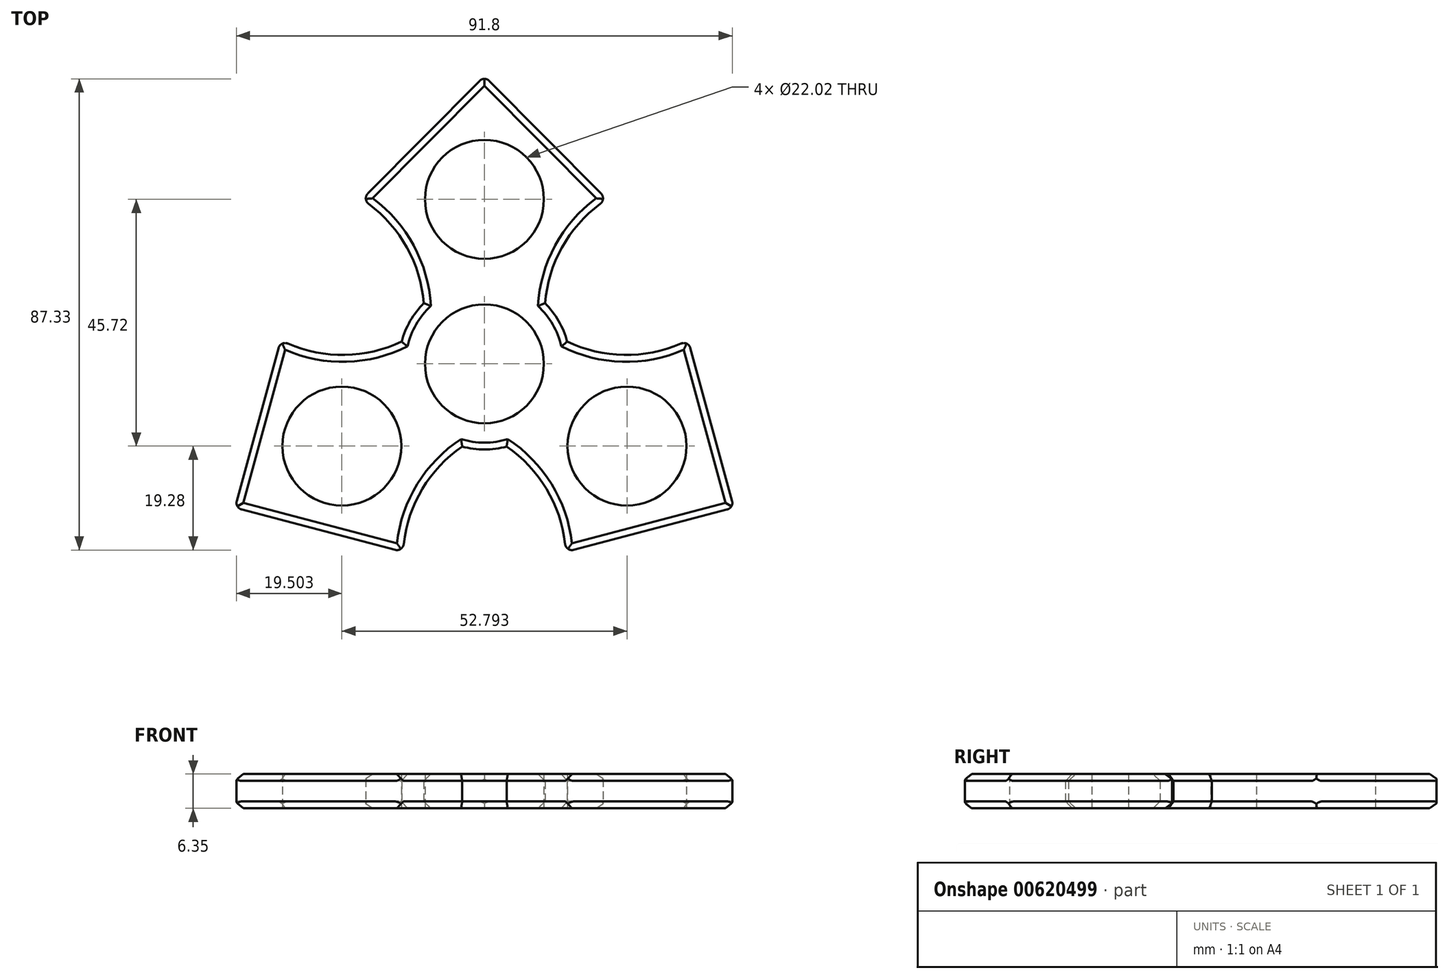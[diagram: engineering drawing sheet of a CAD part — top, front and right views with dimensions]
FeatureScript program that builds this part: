
annotation { "Feature Type Name" : "Feature", "Feature Type Description" : "" }
export const myFeature = defineFeature(function(context is Context, id is Id, definition is map)
    precondition{}
    {
        {
            var Q0;
            Q0=qCreatedBy(makeId("Top.planeOp"),FACE);
            var sketch = newSketch(context, id + "F0", { "sketchPlane" : qUnion([Q0])});
            skCircle(sketch, "E0", {"center": v(0, 0) * mm, "radius": 11.01 * mm});
            skLineSegment(sketch, "E1", {"start": v(0, 0) * mm, "end": v(0, 30.48) * mm});
            skLineSegment(sketch, "E2", {"start": v(0, 0) * mm, "end": v(-26.4, -15.24) * mm});
            skLineSegment(sketch, "E3", {"start": v(0, 0) * mm, "end": v(26.4, -15.24) * mm});
            skCircle(sketch, "E4", {"center": v(0, 0) * mm, "radius": 15.88 * mm});
            skArc(sketch, "E5", {"start": v(-11.23, 11.23) * mm, "mid": v(-14.7, 22.18) * mm, "end": v(-22.65, 30.48) * mm});
            skLineSegment(sketch, "E6", {"start": v(-22.65, 30.48) * mm, "end": v(0, 53.34) * mm});
            skCircle(sketch, "E7", {"center": v(0, 30.48) * mm, "radius": 11.01 * mm});
            skLineSegment(sketch, "E8", {"start": v(0, 53.34) * mm, "end": v(22.65, 30.48) * mm});
            skArc(sketch, "E9", {"start": v(22.65, 30.48) * mm, "mid": v(14.7, 22.18) * mm, "end": v(11.23, 11.23) * mm});
            skLineSegment(sketch, "E10", {"start": v(0, 0) * mm, "end": v(-11.23, 11.23) * mm});
            skLineSegment(sketch, "E11", {"start": v(0, 0) * mm, "end": v(11.23, 11.23) * mm});
            skArc(sketch, "E12.1.0", {"start": v(-4.1, -15.33) * mm, "mid": v(-11.86, -23.82) * mm, "end": v(-15.07, -34.86) * mm});
            skLineSegment(sketch, "E12.1.1", {"start": v(-15.07, -34.86) * mm, "end": v(-46.2, -26.67) * mm});
            skLineSegment(sketch, "E12.1.2", {"start": v(-46.2, -26.67) * mm, "end": v(-37.72, 4.38) * mm});
            skArc(sketch, "E12.1.3", {"start": v(-37.72, 4.38) * mm, "mid": v(-26.56, 1.64) * mm, "end": v(-15.33, 4.1) * mm});
            skCircle(sketch, "E12.1.4", {"center": v(-26.4, -15.24) * mm, "radius": 11.01 * mm});
            skArc(sketch, "E12.2.0", {"start": v(15.33, 4.1) * mm, "mid": v(26.56, 1.64) * mm, "end": v(37.72, 4.38) * mm});
            skLineSegment(sketch, "E12.2.1", {"start": v(37.72, 4.38) * mm, "end": v(46.2, -26.67) * mm});
            skLineSegment(sketch, "E12.2.2", {"start": v(46.2, -26.67) * mm, "end": v(15.07, -34.86) * mm});
            skArc(sketch, "E12.2.3", {"start": v(15.07, -34.86) * mm, "mid": v(11.86, -23.82) * mm, "end": v(4.1, -15.33) * mm});
            skCircle(sketch, "E12.2.4", {"center": v(26.4, -15.24) * mm, "radius": 11.01 * mm});
            skLineSegment(sketch, "E13", {"start": v(0, 53.34) * mm, "end": v(0, 30.48) * mm});
            skLineSegment(sketch, "E14", {"start": v(-29.34, 30.48) * mm, "end": v(31.68, 30.48) * mm});
            skSolve(sketch);
        }
        {
            var Q0;
            {var subQ0=sQuery(id+"F0.wireOp",EDGE,"E12.1.0");Q0=makeQuery(id+"F0.imprint","IMPRINT",FACE,{"disambiguationData":[TD([[makeQuery(id+"F0.imprint","IMPRINT",EDGE,{"derivedFrom":subQ0}),-1.0]])]});}
            var Q1;
            {var subQ0=sQuery(id+"F0.wireOp",EDGE,"E5");Q1=makeQuery(id+"F0.imprint","IMPRINT",FACE,{"disambiguationData":[TD([[makeQuery(id+"F0.imprint","IMPRINT",EDGE,{"derivedFrom":subQ0}),-1.0]])]});}
            var Q2;
            {var subQ0=sQuery(id+"F0.wireOp",EDGE,"E12.2.0");Q2=makeQuery(id+"F0.imprint","IMPRINT",FACE,{"disambiguationData":[TD([[makeQuery(id+"F0.imprint","IMPRINT",EDGE,{"derivedFrom":subQ0}),-1.0]])]});}
            var Q3;
            {var subQ0=sQuery(id+"F0.wireOp",EDGE,"E11");var subQ6=sQuery(id+"F0.wireOp",EDGE,"E0");var subQ8=makeQuery(id+"F0.imprint","INTERSECT",VERTEX,{"derivedFrom":[subQ6,subQ0]});Q3=makeQuery(id+"F0.imprint","IMPRINT",FACE,{"disambiguationData":[TD([[makeQuery(id+"F0.imprint","IMPRINT",EDGE,{"disambiguationData":[TD([[subQ8,1.0]])],"derivedFrom":subQ6}),-1.0]])]});}
            var Q4;
            {var subQ2=sQuery(id+"F0.wireOp",EDGE,"E2");var subQ6=sQuery(id+"F0.wireOp",EDGE,"E0");var subQ8=makeQuery(id+"F0.imprint","INTERSECT",VERTEX,{"derivedFrom":[subQ6,subQ2]});Q4=makeQuery(id+"F0.imprint","IMPRINT",FACE,{"disambiguationData":[TD([[makeQuery(id+"F0.imprint","IMPRINT",EDGE,{"disambiguationData":[TD([[subQ8,-1.0]])],"derivedFrom":subQ6}),-1.0]])]});}
            var Q5;
            {var subQ4=sQuery(id+"F0.wireOp",EDGE,"E10");var subQ6=sQuery(id+"F0.wireOp",EDGE,"E0");var subQ7=makeQuery(id+"F0.imprint","INTERSECT",VERTEX,{"derivedFrom":[subQ6,subQ4]});Q5=makeQuery(id+"F0.imprint","IMPRINT",FACE,{"disambiguationData":[TD([[makeQuery(id+"F0.imprint","IMPRINT",EDGE,{"disambiguationData":[TD([[subQ7,-1.0]])],"derivedFrom":subQ6}),-1.0]])]});}
            var Q6;
            {var subQ0=sQuery(id+"F0.wireOp",EDGE,"E1");var subQ1=sQuery(id+"F0.wireOp",EDGE,"E0");var subQ2=makeQuery(id+"F0.imprint","INTERSECT",VERTEX,{"derivedFrom":[subQ1,subQ0]});Q6=makeQuery(id+"F0.imprint","IMPRINT",FACE,{"disambiguationData":[TD([[makeQuery(id+"F0.imprint","IMPRINT",EDGE,{"disambiguationData":[TD([[subQ2,-1.0]])],"derivedFrom":subQ1}),-1.0]])]});}
            var Q7;
            {var subQ0=sQuery(id+"F0.wireOp",EDGE,"E1");var subQ1=sQuery(id+"F0.wireOp",EDGE,"E0");var subQ2=makeQuery(id+"F0.imprint","INTERSECT",VERTEX,{"derivedFrom":[subQ1,subQ0]});Q7=makeQuery(id+"F0.imprint","IMPRINT",FACE,{"disambiguationData":[TD([[makeQuery(id+"F0.imprint","IMPRINT",EDGE,{"disambiguationData":[TD([[subQ2,1.0]])],"derivedFrom":subQ1}),-1.0]])]});}
            var Q8;
            {var subQ0=sQuery(id+"F0.wireOp",EDGE,"E6");Q8=makeQuery(id+"F0.imprint","IMPRINT",FACE,{"disambiguationData":[TD([[makeQuery(id+"F0.imprint","IMPRINT",EDGE,{"derivedFrom":subQ0}),-1.0]])]});}
            var Q9;
            {var subQ5=sQuery(id+"F0.wireOp",EDGE,"E8");Q9=makeQuery(id+"F0.imprint","IMPRINT",FACE,{"disambiguationData":[TD([[makeQuery(id+"F0.imprint","IMPRINT",EDGE,{"derivedFrom":subQ5}),-1.0]])]});}
            var Q10;
            {var subQ0=sQuery(id+"F0.wireOp",EDGE,"E9");Q10=makeQuery(id+"F0.imprint","IMPRINT",FACE,{"disambiguationData":[TD([[makeQuery(id+"F0.imprint","IMPRINT",EDGE,{"derivedFrom":subQ0}),-1.0]])]});}
            extrude(context, id + "F1", {"entities" : qUnion([Q0, Q1, Q2, Q3, Q4, Q5, Q6, Q7, Q8, Q9, Q10]), "depth" : 6.35 * mm, "offsetDistance" : 25.4 * mm});
        }
        {
            var Q0;
            Q0=makeQuery(id+"F1.opExtrude","CAP_EDGE",EDGE,{"disambiguationData":[OSD([sQuery(id+"F0.wireOp",EDGE,"E12.1.1")])],"isStart":false});
            var Q1;
            Q1=makeQuery(id+"F1.opExtrude","CAP_EDGE",EDGE,{"disambiguationData":[OSD([sQuery(id+"F0.wireOp",EDGE,"E12.1.2")])],"isStart":false});
            var Q2;
            Q2=makeQuery(id+"F1.opExtrude","CAP_EDGE",EDGE,{"disambiguationData":[OSD([sQuery(id+"F0.wireOp",EDGE,"E12.1.0")])],"isStart":false});
            var Q3;
            {var subQ0=sQuery(id+"F0.wireOp",EDGE,"E4");Q3=makeQuery(id+"F1.opExtrude","CAP_EDGE",EDGE,{"disambiguationData":[OSD([subQ0]),TDD([makeQuery(id+"F0.imprint","IMPRINT",EDGE,{"disambiguationData":[TD([[makeQuery(id+"F0.imprint","INTERSECT",VERTEX,{"derivedFrom":[subQ0,sQuery(id+"F0.wireOp",EDGE,"E12.1.0")]}),-1.0]])],"derivedFrom":subQ0})])],"isStart":false});}
            var Q4;
            Q4=makeQuery(id+"F1.opExtrude","CAP_EDGE",EDGE,{"disambiguationData":[OSD([sQuery(id+"F0.wireOp",EDGE,"E12.2.3")])],"isStart":false});
            var Q5;
            {var subQ0=sQuery(id+"F0.wireOp",EDGE,"E4");Q5=makeQuery(id+"F1.opExtrude","CAP_EDGE",EDGE,{"disambiguationData":[OSD([subQ0]),TDD([makeQuery(id+"F0.imprint","IMPRINT",EDGE,{"disambiguationData":[TD([[makeQuery(id+"F0.imprint","INTERSECT",VERTEX,{"derivedFrom":[subQ0,sQuery(id+"F0.wireOp",EDGE,"E12.2.0")]}),-1.0]])],"derivedFrom":subQ0})])],"isStart":false});}
            var Q6;
            Q6=makeQuery(id+"F1.opExtrude","CAP_EDGE",EDGE,{"disambiguationData":[OSD([sQuery(id+"F0.wireOp",EDGE,"E12.2.2")])],"isStart":false});
            var Q7;
            Q7=makeQuery(id+"F1.opExtrude","CAP_EDGE",EDGE,{"disambiguationData":[OSD([sQuery(id+"F0.wireOp",EDGE,"E12.2.1")])],"isStart":false});
            var Q8;
            Q8=makeQuery(id+"F1.opExtrude","CAP_EDGE",EDGE,{"disambiguationData":[OSD([sQuery(id+"F0.wireOp",EDGE,"E12.2.0")])],"isStart":false});
            var Q9;
            Q9=makeQuery(id+"F1.opExtrude","CAP_EDGE",EDGE,{"disambiguationData":[OSD([sQuery(id+"F0.wireOp",EDGE,"E9")])],"isStart":false});
            var Q10;
            Q10=makeQuery(id+"F1.opExtrude","CAP_EDGE",EDGE,{"disambiguationData":[OSD([sQuery(id+"F0.wireOp",EDGE,"E8")])],"isStart":false});
            var Q11;
            Q11=makeQuery(id+"F1.opExtrude","CAP_EDGE",EDGE,{"disambiguationData":[OSD([sQuery(id+"F0.wireOp",EDGE,"E6")])],"isStart":false});
            var Q12;
            Q12=makeQuery(id+"F1.opExtrude","CAP_EDGE",EDGE,{"disambiguationData":[OSD([sQuery(id+"F0.wireOp",EDGE,"E5")])],"isStart":false});
            var Q13;
            Q13=makeQuery(id+"F1.opExtrude","CAP_EDGE",EDGE,{"disambiguationData":[OSD([sQuery(id+"F0.wireOp",EDGE,"E12.1.3")])],"isStart":false});
            var Q14;
            {var subQ0=sQuery(id+"F0.wireOp",EDGE,"E4");Q14=makeQuery(id+"F1.opExtrude","CAP_EDGE",EDGE,{"disambiguationData":[OSD([subQ0]),TDD([makeQuery(id+"F0.imprint","IMPRINT",EDGE,{"disambiguationData":[TD([[makeQuery(id+"F0.imprint","INTERSECT",VERTEX,{"derivedFrom":[subQ0,sQuery(id+"F0.wireOp",EDGE,"E12.1.3")]}),1.0]])],"derivedFrom":subQ0})])],"isStart":false});}
            chamfer(context, id + "F2", {"entities" : qUnion([Q0, Q1, Q2, Q3, Q4, Q5, Q6, Q7, Q8, Q9, Q10, Q11, Q12, Q13, Q14]), "width" : 1.27 * mm, "tangentPropagation" : true});
        }
        {
            var Q0;
            Q0=makeQuery(id+"F1.opExtrude","CAP_EDGE",EDGE,{"disambiguationData":[OSD([sQuery(id+"F0.wireOp",EDGE,"E12.1.1")])],"isStart":true});
            var Q1;
            Q1=makeQuery(id+"F1.opExtrude","CAP_EDGE",EDGE,{"disambiguationData":[OSD([sQuery(id+"F0.wireOp",EDGE,"E12.1.2")])],"isStart":true});
            var Q2;
            Q2=makeQuery(id+"F1.opExtrude","CAP_EDGE",EDGE,{"disambiguationData":[OSD([sQuery(id+"F0.wireOp",EDGE,"E12.1.3")])],"isStart":true});
            var Q3;
            Q3=makeQuery(id+"F1.opExtrude","CAP_EDGE",EDGE,{"disambiguationData":[OSD([sQuery(id+"F0.wireOp",EDGE,"E5")])],"isStart":true});
            var Q4;
            Q4=makeQuery(id+"F1.opExtrude","CAP_EDGE",EDGE,{"disambiguationData":[OSD([sQuery(id+"F0.wireOp",EDGE,"E6")])],"isStart":true});
            var Q5;
            Q5=makeQuery(id+"F1.opExtrude","CAP_EDGE",EDGE,{"disambiguationData":[OSD([sQuery(id+"F0.wireOp",EDGE,"E8")])],"isStart":true});
            var Q6;
            Q6=makeQuery(id+"F1.opExtrude","CAP_EDGE",EDGE,{"disambiguationData":[OSD([sQuery(id+"F0.wireOp",EDGE,"E9")])],"isStart":true});
            var Q7;
            Q7=makeQuery(id+"F1.opExtrude","CAP_EDGE",EDGE,{"disambiguationData":[OSD([sQuery(id+"F0.wireOp",EDGE,"E12.2.0")])],"isStart":true});
            var Q8;
            Q8=makeQuery(id+"F1.opExtrude","CAP_EDGE",EDGE,{"disambiguationData":[OSD([sQuery(id+"F0.wireOp",EDGE,"E12.2.1")])],"isStart":true});
            var Q9;
            Q9=makeQuery(id+"F1.opExtrude","CAP_EDGE",EDGE,{"disambiguationData":[OSD([sQuery(id+"F0.wireOp",EDGE,"E12.2.2")])],"isStart":true});
            var Q10;
            Q10=makeQuery(id+"F1.opExtrude","CAP_EDGE",EDGE,{"disambiguationData":[OSD([sQuery(id+"F0.wireOp",EDGE,"E12.2.3")])],"isStart":true});
            var Q11;
            Q11=makeQuery(id+"F1.opExtrude","CAP_EDGE",EDGE,{"disambiguationData":[OSD([sQuery(id+"F0.wireOp",EDGE,"E12.1.0")])],"isStart":true});
            var Q12;
            {var subQ0=sQuery(id+"F0.wireOp",EDGE,"E4");Q12=makeQuery(id+"F1.opExtrude","CAP_EDGE",EDGE,{"disambiguationData":[OSD([subQ0]),TDD([makeQuery(id+"F0.imprint","IMPRINT",EDGE,{"disambiguationData":[TD([[makeQuery(id+"F0.imprint","INTERSECT",VERTEX,{"derivedFrom":[subQ0,sQuery(id+"F0.wireOp",EDGE,"E12.1.0")]}),-1.0]])],"derivedFrom":subQ0})])],"isStart":true});}
            var Q13;
            {var subQ0=sQuery(id+"F0.wireOp",EDGE,"E4");Q13=makeQuery(id+"F1.opExtrude","CAP_EDGE",EDGE,{"disambiguationData":[OSD([subQ0]),TDD([makeQuery(id+"F0.imprint","IMPRINT",EDGE,{"disambiguationData":[TD([[makeQuery(id+"F0.imprint","INTERSECT",VERTEX,{"derivedFrom":[subQ0,sQuery(id+"F0.wireOp",EDGE,"E12.1.3")]}),1.0]])],"derivedFrom":subQ0})])],"isStart":true});}
            var Q14;
            {var subQ0=sQuery(id+"F0.wireOp",EDGE,"E4");Q14=makeQuery(id+"F1.opExtrude","CAP_EDGE",EDGE,{"disambiguationData":[OSD([subQ0]),TDD([makeQuery(id+"F0.imprint","IMPRINT",EDGE,{"disambiguationData":[TD([[makeQuery(id+"F0.imprint","INTERSECT",VERTEX,{"derivedFrom":[subQ0,sQuery(id+"F0.wireOp",EDGE,"E12.2.0")]}),-1.0]])],"derivedFrom":subQ0})])],"isStart":true});}
            chamfer(context, id + "F3", {"entities" : qUnion([Q0, Q1, Q2, Q3, Q4, Q5, Q6, Q7, Q8, Q9, Q10, Q11, Q12, Q13, Q14]), "width" : 1.27 * mm, "tangentPropagation" : true});
        }
        {
            var Q0;
            Q0=makeQuery(id+"F1.opExtrude","SWEPT_EDGE",EDGE,{"disambiguationData":[OSD([sQuery(id+"F0.wireOp",EDGE,"E12.2.1"),sQuery(id+"F0.wireOp",EDGE,"E12.2.2")])]});
            var Q1;
            Q1=makeQuery(id+"F1.opExtrude","SWEPT_EDGE",EDGE,{"disambiguationData":[OSD([sQuery(id+"F0.wireOp",EDGE,"E12.2.0"),sQuery(id+"F0.wireOp",EDGE,"E12.2.1")])]});
            var Q2;
            Q2=makeQuery(id+"F1.opExtrude","SWEPT_EDGE",EDGE,{"disambiguationData":[OSD([sQuery(id+"F0.wireOp",EDGE,"E8"),sQuery(id+"F0.wireOp",EDGE,"E9")])]});
            var Q3;
            Q3=makeQuery(id+"F1.opExtrude","SWEPT_EDGE",EDGE,{"disambiguationData":[OSD([sQuery(id+"F0.wireOp",EDGE,"E6"),sQuery(id+"F0.wireOp",EDGE,"E8")])]});
            var Q4;
            Q4=makeQuery(id+"F1.opExtrude","SWEPT_EDGE",EDGE,{"disambiguationData":[OSD([sQuery(id+"F0.wireOp",EDGE,"E5"),sQuery(id+"F0.wireOp",EDGE,"E6")])]});
            var Q5;
            Q5=makeQuery(id+"F1.opExtrude","SWEPT_EDGE",EDGE,{"disambiguationData":[OSD([sQuery(id+"F0.wireOp",EDGE,"E12.1.2"),sQuery(id+"F0.wireOp",EDGE,"E12.1.3")])]});
            var Q6;
            Q6=makeQuery(id+"F1.opExtrude","SWEPT_EDGE",EDGE,{"disambiguationData":[OSD([sQuery(id+"F0.wireOp",EDGE,"E12.1.1"),sQuery(id+"F0.wireOp",EDGE,"E12.1.2")])]});
            var Q7;
            Q7=makeQuery(id+"F1.opExtrude","SWEPT_EDGE",EDGE,{"disambiguationData":[OSD([sQuery(id+"F0.wireOp",EDGE,"E12.1.0"),sQuery(id+"F0.wireOp",EDGE,"E12.1.1")])]});
            var Q8;
            Q8=makeQuery(id+"F1.opExtrude","SWEPT_EDGE",EDGE,{"disambiguationData":[OSD([sQuery(id+"F0.wireOp",EDGE,"E12.2.2"),sQuery(id+"F0.wireOp",EDGE,"E12.2.3")])]});
            fillet(context, id + "F4", {"entities" : qUnion([Q0, Q1, Q2, Q3, Q4, Q5, Q6, Q7, Q8]), "radius" : 1.27 * mm, "tangentPropagation" : true, "allowEdgeOverflow" : false});
        }
    });
